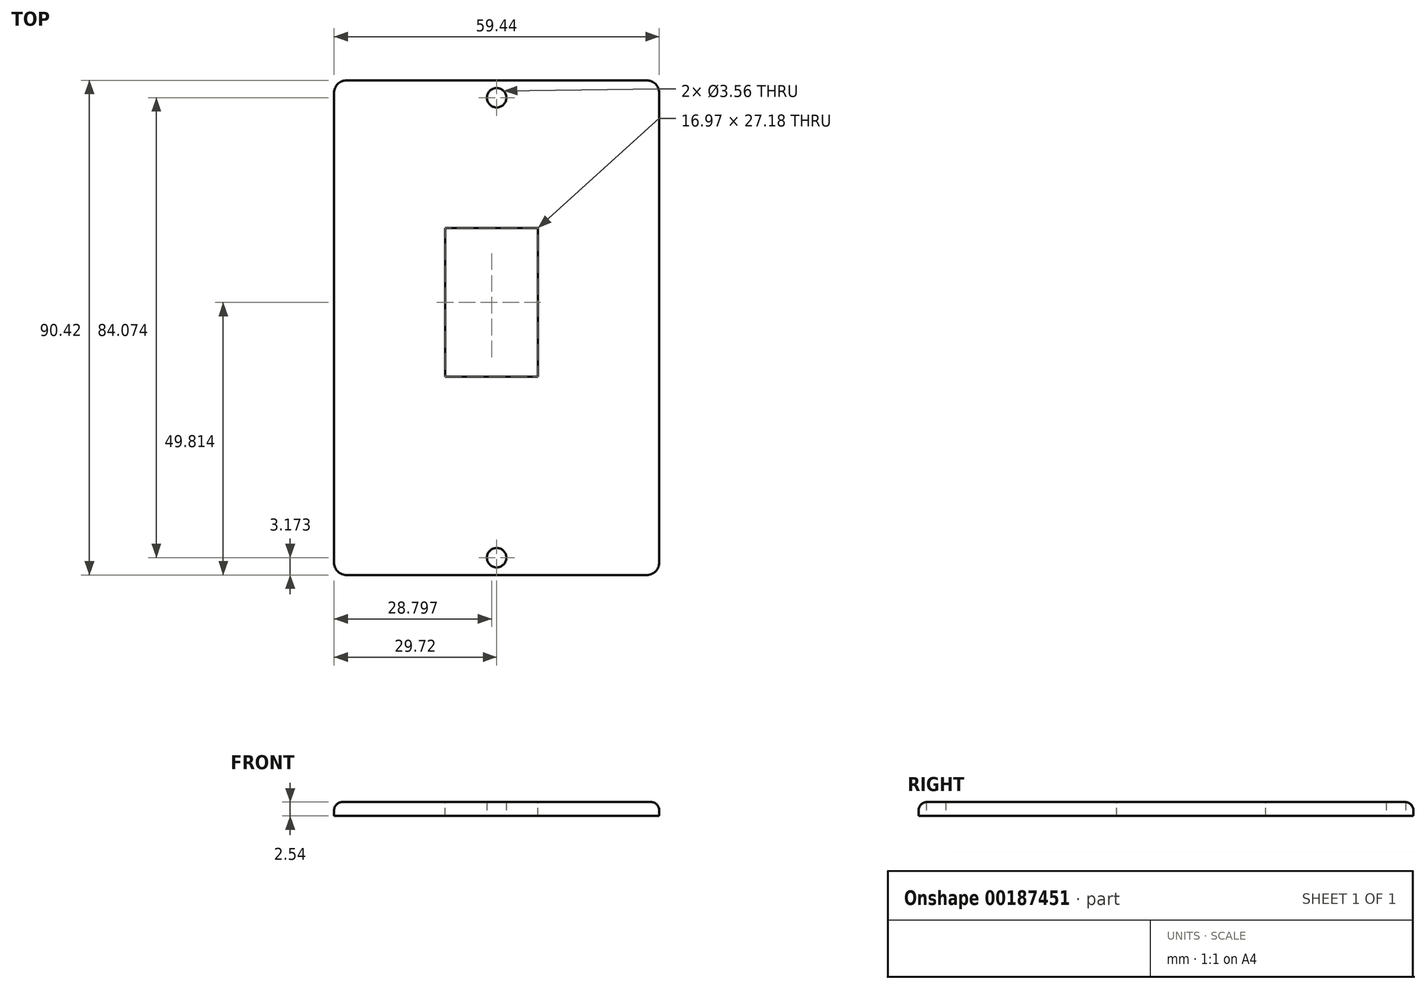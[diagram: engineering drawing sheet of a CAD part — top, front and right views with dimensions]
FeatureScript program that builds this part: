
annotation { "Feature Type Name" : "Feature", "Feature Type Description" : "" }
export const myFeature = defineFeature(function(context is Context, id is Id, definition is map)
    precondition{}
    {
        {
            var Q0;
            Q0=qCreatedBy(makeId("Top.planeOp"),FACE);
            var sketch = newSketch(context, id + "F0", { "sketchPlane" : qUnion([Q0])});
            skLineSegment(sketch, "E0.bottom", {"start": v(29.72, 45.21) * mm, "end": v(-29.72, 45.21) * mm});
            skLineSegment(sketch, "E0.top", {"start": v(29.72, -45.21) * mm, "end": v(-29.72, -45.21) * mm});
            skLineSegment(sketch, "E0.left", {"start": v(29.72, 45.21) * mm, "end": v(29.72, -45.21) * mm});
            skLineSegment(sketch, "E0.right", {"start": v(-29.72, 45.21) * mm, "end": v(-29.72, -45.21) * mm});
            skPoint(sketch, "E0.middle", {"position": v(0, 0) * mm});
            skSolve(sketch);
        }
        {
            var Q0;
            Q0=makeQuery(id+"F0.imprint","IMPRINT",FACE,{"disambiguationData":[TD([[makeQuery(id+"F0.imprint","IMPRINT",EDGE,{"derivedFrom":sQuery(id+"F0.wireOp",EDGE,"E0.bottom")}),1.0]])]});
            extrude(context, id + "F1", {"entities" : qUnion([Q0]), "depth" : 2.54 * mm});
        }
        {
            var Q0;
            Q0=makeQuery(id+"F1.opExtrude","SWEPT_EDGE",EDGE,{"disambiguationData":[OSD([sQuery(id+"F0.wireOp",EDGE,"E0.top"),sQuery(id+"F0.wireOp",EDGE,"E0.left")])]});
            var Q1;
            Q1=makeQuery(id+"F1.opExtrude","SWEPT_EDGE",EDGE,{"disambiguationData":[OSD([sQuery(id+"F0.wireOp",EDGE,"E0.top"),sQuery(id+"F0.wireOp",EDGE,"E0.right")])]});
            var Q2;
            Q2=makeQuery(id+"F1.opExtrude","SWEPT_EDGE",EDGE,{"disambiguationData":[OSD([sQuery(id+"F0.wireOp",EDGE,"E0.bottom"),sQuery(id+"F0.wireOp",EDGE,"E0.left")])]});
            var Q3;
            Q3=makeQuery(id+"F1.opExtrude","SWEPT_EDGE",EDGE,{"disambiguationData":[OSD([sQuery(id+"F0.wireOp",EDGE,"E0.bottom"),sQuery(id+"F0.wireOp",EDGE,"E0.right")])]});
            fillet(context, id + "F2", {"entities" : qUnion([Q0, Q1, Q2, Q3]), "radius" : 2.3 * mm, "tangentPropagation" : true, "allowEdgeOverflow" : false});
        }
        {
            var Q0;
            Q0=makeQuery(id+"F1.opExtrude","CAP_EDGE",EDGE,{"disambiguationData":[OSD([sQuery(id+"F0.wireOp",EDGE,"E0.right")])],"isStart":false});
            fillet(context, id + "F3", {"entities" : qUnion([Q0]), "radius" : 1.52 * mm, "tangentPropagation" : true, "allowEdgeOverflow" : false});
        }
        {
            var Q0;
            Q0=makeQuery(id+"F1.opExtrude","CAP_FACE",FACE,{"disambiguationData":[OSD([sQuery(id+"F0.wireOp",EDGE,"E0.bottom"),sQuery(id+"F0.wireOp",EDGE,"E0.top"),sQuery(id+"F0.wireOp",EDGE,"E0.left"),sQuery(id+"F0.wireOp",EDGE,"E0.right")])],"isStart":true});
            var sketch = newSketch(context, id + "F4", { "sketchPlane" : qUnion([Q0])});
            skCircle(sketch, "E1", {"center": v(0, 42.04) * mm, "radius": 1.78 * mm});
            skCircle(sketch, "E2", {"center": v(0, -42.04) * mm, "radius": 1.78 * mm});
            skSolve(sketch);
        }
        {
            var Q0;
            Q0=makeQuery(id+"F4.imprint","IMPRINT",FACE,{"disambiguationData":[TD([[makeQuery(id+"F4.imprint","IMPRINT",EDGE,{"derivedFrom":sQuery(id+"F4.wireOp",EDGE,"E1")}),1.0]])]});
            var Q1;
            Q1=makeQuery(id+"F4.imprint","IMPRINT",FACE,{"disambiguationData":[TD([[makeQuery(id+"F4.imprint","IMPRINT",EDGE,{"derivedFrom":sQuery(id+"F4.wireOp",EDGE,"E2")}),1.0]])]});
            extrude(context, id + "F5", {"entities" : qUnion([Q0, Q1]), "operationType" : NewBodyOperationType.REMOVE, "oppositeDirection" : true, "depth" : 25.4 * mm});
        }
        {
            var Q0;
            Q0=makeQuery(id+"F1.opExtrude","CAP_FACE",FACE,{"disambiguationData":[OSD([sQuery(id+"F0.wireOp",EDGE,"E0.bottom"),sQuery(id+"F0.wireOp",EDGE,"E0.top"),sQuery(id+"F0.wireOp",EDGE,"E0.left"),sQuery(id+"F0.wireOp",EDGE,"E0.right")])],"isStart":false});
            var sketch = newSketch(context, id + "F6", { "sketchPlane" : qUnion([Q0])});
            skLineSegment(sketch, "E3.bottom", {"start": v(7.56, 18.2) * mm, "end": v(-9.4, 18.2) * mm});
            skLineSegment(sketch, "E3.top", {"start": v(7.56, -8.99) * mm, "end": v(-9.4, -8.99) * mm});
            skLineSegment(sketch, "E3.left", {"start": v(7.56, 18.2) * mm, "end": v(7.56, -8.99) * mm});
            skLineSegment(sketch, "E3.right", {"start": v(-9.4, 18.2) * mm, "end": v(-9.4, -8.99) * mm});
            skPoint(sketch, "E3.middle", {"position": v(-0.92, 4.6) * mm});
            skSolve(sketch);
        }
        {
            var Q0;
            Q0=makeQuery(id+"F6.imprint","IMPRINT",FACE,{"disambiguationData":[TD([[makeQuery(id+"F6.imprint","IMPRINT",EDGE,{"derivedFrom":sQuery(id+"F6.wireOp",EDGE,"E3.bottom")}),1.0]])]});
            extrude(context, id + "F7", {"entities" : qUnion([Q0]), "operationType" : NewBodyOperationType.REMOVE, "oppositeDirection" : true, "depth" : 25.4 * mm});
        }
    });
